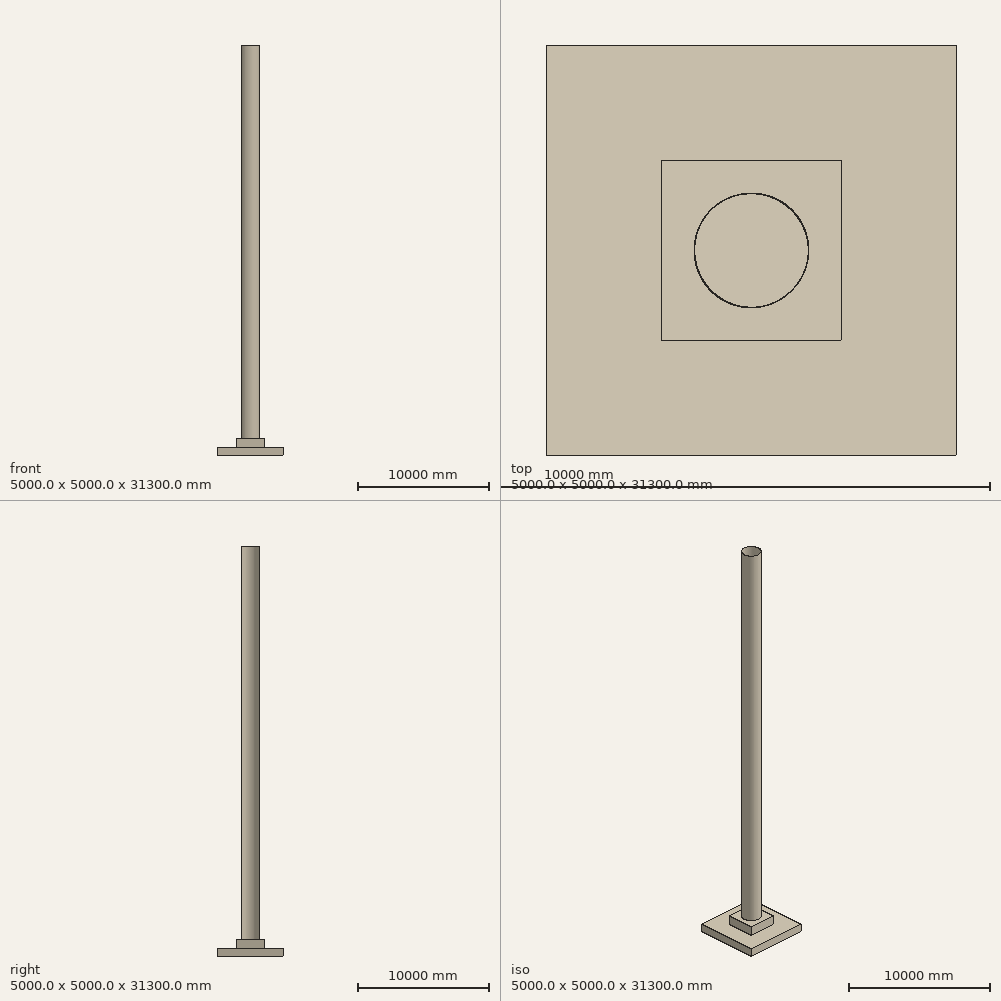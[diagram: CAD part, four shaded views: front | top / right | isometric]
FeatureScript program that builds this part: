
annotation { "Feature Type Name" : "Feature", "Feature Type Description" : "" }
export const myFeature = defineFeature(function(context is Context, id is Id, definition is map)
    precondition{}
    {
        {
            var Q0;
            Q0=qCreatedBy(makeId("Top.planeOp"),FACE);
            var sketch = newSketch(context, id + "F0", { "sketchPlane" : qUnion([Q0])});
            skLineSegment(sketch, "E0.bottom", {"start": v(-2500, 2500) * mm, "end": v(2500, 2500) * mm});
            skLineSegment(sketch, "E0.top", {"start": v(-2500, -2500) * mm, "end": v(2500, -2500) * mm});
            skLineSegment(sketch, "E0.left", {"start": v(-2500, 2500) * mm, "end": v(-2500, -2500) * mm});
            skLineSegment(sketch, "E0.right", {"start": v(2500, 2500) * mm, "end": v(2500, -2500) * mm});
            skSolve(sketch);
        }
        {
            var Q0;
            Q0=makeQuery(id+"F0.imprint","IMPRINT",FACE,{"disambiguationData":[TD([[makeQuery(id+"F0.imprint","IMPRINT",EDGE,{"derivedFrom":sQuery(id+"F0.wireOp",EDGE,"E0.bottom")}),-1.0]])]});
            extrude(context, id + "F1", {"entities" : qUnion([Q0]), "depth" : 600 * mm});
        }
        {
            var Q0;
            Q0=makeQuery(id+"F1.opExtrude","CAP_FACE",FACE,{"disambiguationData":[OSD([sQuery(id+"F0.wireOp",EDGE,"E0.bottom"),sQuery(id+"F0.wireOp",EDGE,"E0.top"),sQuery(id+"F0.wireOp",EDGE,"E0.left"),sQuery(id+"F0.wireOp",EDGE,"E0.right")])],"isStart":false});
            var sketch = newSketch(context, id + "F2", { "sketchPlane" : qUnion([Q0])});
            skLineSegment(sketch, "E1.bottom", {"start": v(-1100, 1100) * mm, "end": v(1100, 1100) * mm});
            skLineSegment(sketch, "E1.top", {"start": v(-1100, -1100) * mm, "end": v(1100, -1100) * mm});
            skLineSegment(sketch, "E1.left", {"start": v(-1100, 1100) * mm, "end": v(-1100, -1100) * mm});
            skLineSegment(sketch, "E1.right", {"start": v(1100, 1100) * mm, "end": v(1100, -1100) * mm});
            skSolve(sketch);
        }
        {
            var Q0;
            Q0=makeQuery(id+"F2.imprint","IMPRINT",FACE,{"disambiguationData":[TD([[makeQuery(id+"F2.imprint","IMPRINT",EDGE,{"derivedFrom":sQuery(id+"F2.wireOp",EDGE,"E1.bottom")}),-1.0]])]});
            extrude(context, id + "F3", {"entities" : qUnion([Q0]), "operationType" : NewBodyOperationType.ADD, "depth" : 700 * mm});
        }
        {
            var Q0;
            Q0=makeQuery(id+"F3.opExtrude","CAP_FACE",FACE,{"disambiguationData":[OSD([sQuery(id+"F2.wireOp",EDGE,"E1.bottom"),sQuery(id+"F2.wireOp",EDGE,"E1.top"),sQuery(id+"F2.wireOp",EDGE,"E1.left"),sQuery(id+"F2.wireOp",EDGE,"E1.right")])],"isStart":false});
            var sketch = newSketch(context, id + "F4", { "sketchPlane" : qUnion([Q0])});
            skCircle(sketch, "E2", {"center": v(0, 0) * mm, "radius": 700 * mm});
            skCircle(sketch, "E3.0", {"center": v(0, 0) * mm, "radius": 692 * mm});
            skSolve(sketch);
        }
        {
            var Q0;
            Q0=makeQuery(id+"F4.imprint","IMPRINT",FACE,{"disambiguationData":[TD([[makeQuery(id+"F4.imprint","IMPRINT",EDGE,{"derivedFrom":sQuery(id+"F4.wireOp",EDGE,"E2")}),1.0]])]});
            extrude(context, id + "F5", {"entities" : qUnion([Q0]), "operationType" : NewBodyOperationType.ADD, "depth" : 30000 * mm});
        }
    });
